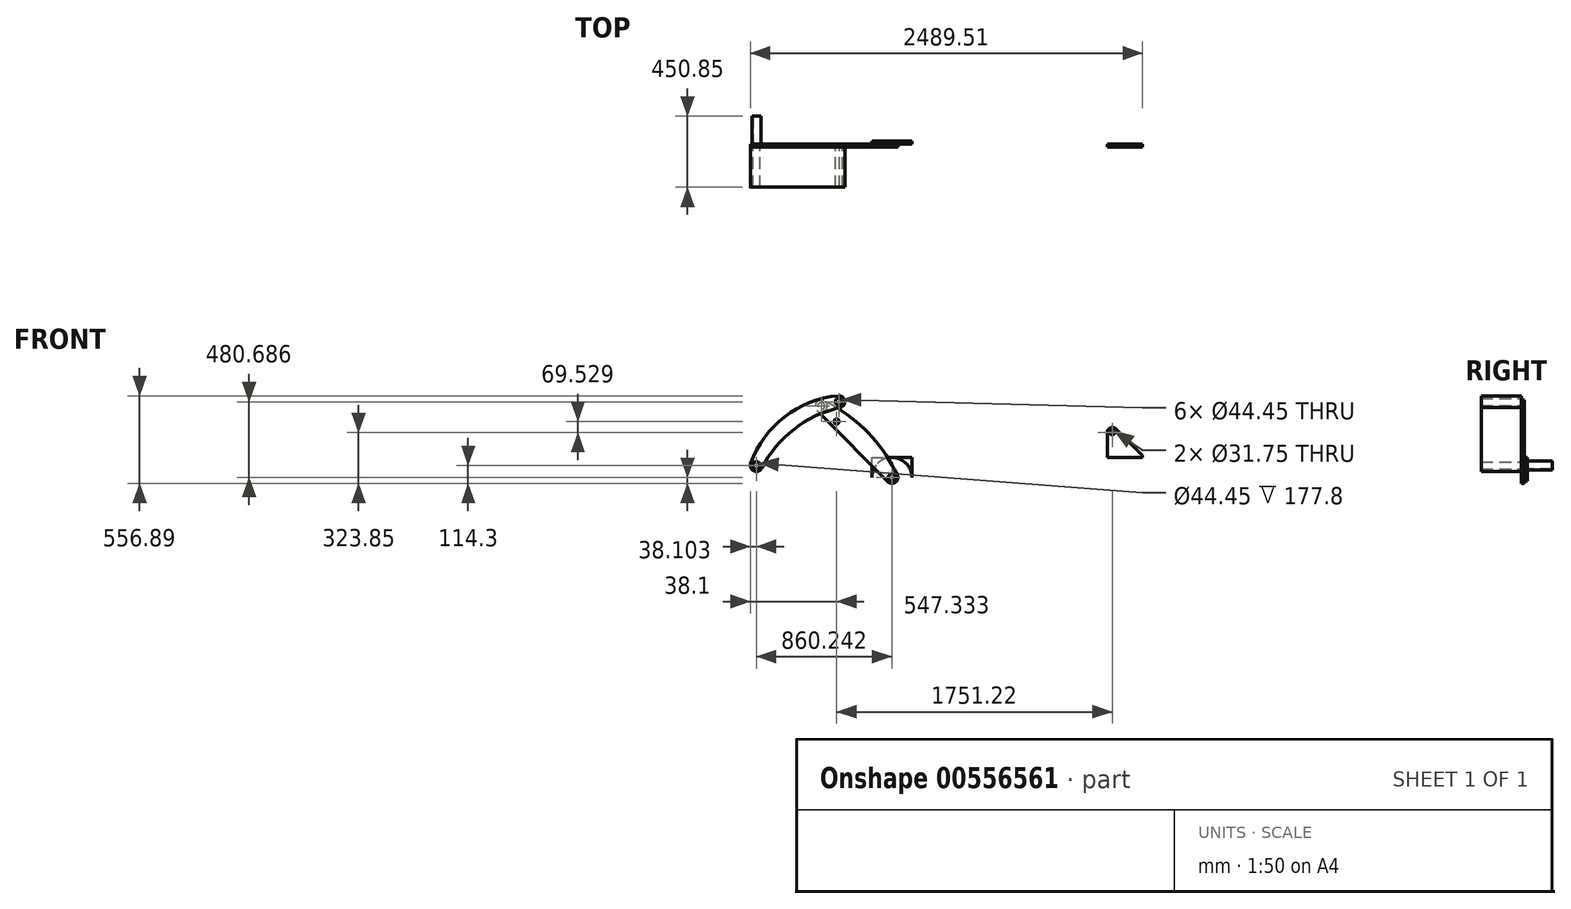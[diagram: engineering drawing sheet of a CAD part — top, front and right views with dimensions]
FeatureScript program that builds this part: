
annotation { "Feature Type Name" : "Feature", "Feature Type Description" : "" }
export const myFeature = defineFeature(function(context is Context, id is Id, definition is map)
    precondition{}
    {
        {
            var Q0;
            Q0=qCreatedBy(makeId("Front.planeOp"),FACE);
            var sketch = newSketch(context, id + "F0", { "sketchPlane" : qUnion([Q0])});
            skLineSegment(sketch, "E0.bottom", {"start": v(-1348.74, 177.8) * mm, "end": v(-129.54, 177.8) * mm, "construction": true});
            skLineSegment(sketch, "E0.top", {"start": v(-1348.74, 0) * mm, "end": v(-129.54, 0) * mm, "construction": true});
            skLineSegment(sketch, "E0.left", {"start": v(-1348.74, 177.8) * mm, "end": v(-1348.74, 0) * mm, "construction": true});
            skLineSegment(sketch, "E0.right", {"start": v(-129.54, 177.8) * mm, "end": v(-129.54, 0) * mm, "construction": true});
            skLineSegment(sketch, "E1.bottom", {"start": v(0, 177.8) * mm, "end": v(1219.2, 177.8) * mm, "construction": true});
            skLineSegment(sketch, "E1.top", {"start": v(0, 0) * mm, "end": v(1219.2, 0) * mm, "construction": true});
            skLineSegment(sketch, "E1.left", {"start": v(0, 177.8) * mm, "end": v(0, 0) * mm, "construction": true});
            skLineSegment(sketch, "E1.right", {"start": v(1219.2, 177.8) * mm, "end": v(1219.2, 0) * mm, "construction": true});
            skPoint(sketch, "E2", {"position": v(-64.77, 279.4) * mm});
            skPoint(sketch, "E3", {"position": v(-477, 127) * mm});
            skPoint(sketch, "E4", {"position": v(383.24, 50.8) * mm});
            skPoint(sketch, "E5", {"position": v(-64.77, 504.25) * mm});
            skCircle(sketch, "E6", {"center": v(-477, 127) * mm, "radius": 28.58 * mm, "construction": true});
            skCircle(sketch, "E7", {"center": v(383.24, 50.8) * mm, "radius": 28.58 * mm, "construction": true});
            skLineSegment(sketch, "E8", {"start": v(-477, 127) * mm, "end": v(-64.77, 504.25) * mm, "construction": true});
            skPoint(sketch, "E9", {"position": v(32.22, 406.08) * mm});
            skLineSegment(sketch, "E10", {"start": v(-64.77, 279.4) * mm, "end": v(-477, 127) * mm, "construction": true});
            skLineSegment(sketch, "E11", {"start": v(-64.77, 279.4) * mm, "end": v(347.47, 431.8) * mm, "construction": true});
            skLineSegment(sketch, "E12", {"start": v(347.47, 431.8) * mm, "end": v(906.03, 415.5) * mm, "construction": true});
            skPoint(sketch, "E13", {"position": v(792.84, 336.55) * mm});
            skLineSegment(sketch, "E14", {"start": v(792.84, 336.55) * mm, "end": v(1783.44, 336.55) * mm, "construction": true});
            skLineSegment(sketch, "E15", {"start": v(1783.44, 336.55) * mm, "end": v(32.22, 406.08) * mm, "construction": true});
            skLineSegment(sketch, "E16", {"start": v(906.03, 415.5) * mm, "end": v(792.84, 336.55) * mm, "construction": true});
            skLineSegment(sketch, "E17", {"start": v(792.84, 336.55) * mm, "end": v(383.24, 50.8) * mm, "construction": true});
            skLineSegment(sketch, "E18", {"start": v(383.24, 50.8) * mm, "end": v(32.22, 406.08) * mm, "construction": true});
            skLineSegment(sketch, "E19", {"start": v(32.22, 406.08) * mm, "end": v(-64.77, 504.25) * mm, "construction": true});
            skSolve(sketch);
        }
        {
            var Q0;
            Q0=qCreatedBy(makeId("Front.planeOp"),FACE);
            var sketch = newSketch(context, id + "F1", { "sketchPlane" : qUnion([Q0])});
            skCircle(sketch, "E20", {"center": v(-477, 127) * mm, "radius": 22.23 * mm});
            skCircle(sketch, "E21", {"center": v(-477, 127) * mm, "radius": 28.58 * mm});
            skSolve(sketch);
        }
        {
            var Q0;
            Q0 = qSketchRegion(id + "F1", true);
            extrude(context, id + "F2", {"entities" : qUnion([Q0]), "oppositeDirection" : true, "depth" : 177.8 * mm, "offsetDistance" : 25.4 * mm});
        }
        {
            var Q0;
            Q0=qCreatedBy(makeId("Front.planeOp"),FACE);
            var sketch = newSketch(context, id + "F3", { "sketchPlane" : qUnion([Q0])});
            skCircle(sketch, "E22", {"center": v(383.24, 50.8) * mm, "radius": 22.23 * mm});
            skArc(sketch, "E23", {"start": v(256.24, 50.8) * mm, "mid": v(383.24, 177.8) * mm, "end": v(510.24, 50.8) * mm});
            skLineSegment(sketch, "E24", {"start": v(510.24, 177.8) * mm, "end": v(510.24, 50.8) * mm});
            skLineSegment(sketch, "E25", {"start": v(256.24, 177.8) * mm, "end": v(510.24, 177.8) * mm});
            skLineSegment(sketch, "E26", {"start": v(256.24, 50.8) * mm, "end": v(256.24, 177.8) * mm});
            skSolve(sketch);
        }
        {
            var Q0;
            Q0 = qSketchRegion(id + "F3", true);
            extrude(context, id + "F4", {"entities" : qUnion([Q0]), "oppositeDirection" : true, "depth" : 19.05 * mm, "offsetDistance" : 25.4 * mm});
        }
        {
            var Q0;
            Q0=qCreatedBy(makeId("Front.planeOp"),FACE);
            var sketch = newSketch(context, id + "F5", { "sketchPlane" : qUnion([Q0])});
            skCircle(sketch, "E27", {"center": v(383.24, 50.8) * mm, "radius": 22.23 * mm});
            skArc(sketch, "E28", {"start": v(356.13, 24.02) * mm, "mid": v(405.17, 19.65) * mm, "end": v(417.59, 67.28) * mm});
            skCircle(sketch, "E29", {"center": v(32.22, 406.08) * mm, "radius": 15.88 * mm});
            skLineSegment(sketch, "E30.trimOffspring", {"start": v(146.95, 412.86) * mm, "end": v(146.95, 412.86) * mm});
            skArc(sketch, "E31", {"start": v(-47.87, 538.4) * mm, "mid": v(-95.66, 526.56) * mm, "end": v(-91.87, 477.47) * mm});
            skLineSegment(sketch, "E32", {"start": v(-91.87, 477.47) * mm, "end": v(356.13, 24.02) * mm});
            skCircle(sketch, "E33", {"center": v(-64.77, 504.25) * mm, "radius": 22.23 * mm});
            skArc(sketch, "E34", {"start": v(417.59, 67.28) * mm, "mid": v(224.32, 341.83) * mm, "end": v(-47.87, 538.4) * mm});
            skSolve(sketch);
        }
        {
            var Q0;
            Q0 = qSketchRegion(id + "F5", true);
            extrude(context, id + "F6", {"entities" : qUnion([Q0]), "depth" : 19.05 * mm, "offsetDistance" : 25.4 * mm});
        }
        {
            var Q0;
            Q0=qCreatedBy(makeId("Front.planeOp"),FACE);
            var sketch = newSketch(context, id + "F7", { "sketchPlane" : qUnion([Q0])});
            skCircle(sketch, "E35", {"center": v(-477, 127) * mm, "radius": 22.23 * mm});
            skCircle(sketch, "E36", {"center": v(-64.77, 504.25) * mm, "radius": 22.23 * mm});
            skArc(sketch, "E37", {"start": v(-512.9, 139.8) * mm, "mid": v(-492.12, 92.02) * mm, "end": v(-443.09, 109.64) * mm});
            skArc(sketch, "E38", {"start": v(-50.48, 468.93) * mm, "mid": v(-28.6, 516.2) * mm, "end": v(-74.34, 541.13) * mm});
            skArc(sketch, "E39", {"start": v(-74.34, 541.13) * mm, "mid": v(-343.48, 394.95) * mm, "end": v(-512.9, 139.8) * mm});
            skArc(sketch, "E40", {"start": v(-50.48, 468.93) * mm, "mid": v(-279.17, 324.68) * mm, "end": v(-443.09, 109.64) * mm});
            skLineSegment(sketch, "E41", {"start": v(847.43, 417.22) * mm, "end": v(780, 419.19) * mm, "construction": true});
            skLineSegment(sketch, "E42", {"start": v(847.43, 417.22) * mm, "end": v(906.03, 415.5) * mm, "construction": true});
            skCircle(sketch, "E43", {"center": v(-146.1, 406.71) * mm, "radius": 38.1 * mm, "construction": true});
            skLineSegment(sketch, "E44", {"start": v(-132.47, 442.3) * mm, "end": v(-182.75, 396.28) * mm, "construction": true});
            skLineSegment(sketch, "E45", {"start": v(-132.47, 442.3) * mm, "end": v(-43.7, 523.53) * mm, "construction": true});
            skSolve(sketch);
        }
        {
            var Q0;
            Q0 = qSketchRegion(id + "F7", true);
            extrude(context, id + "F8", {"entities" : qUnion([Q0]), "depth" : 19.05 * mm, "offsetDistance" : 25.4 * mm});
        }
        {
            var Q0;
            Q0=makeQuery(id+"F8.opExtrude","CAP_FACE",FACE,{"disambiguationData":[OSD([sQuery(id+"F7.wireOp",EDGE,"E36"),sQuery(id+"F7.wireOp",EDGE,"E37"),sQuery(id+"F7.wireOp",EDGE,"E38"),sQuery(id+"F7.wireOp",EDGE,"E39"),sQuery(id+"F7.wireOp",EDGE,"E40"),sQuery(id+"F7.wireOp",EDGE,"E35")])],"isStart":false});
            var sketch = newSketch(context, id + "F9", { "sketchPlane" : qUnion([Q0])});
            skCircle(sketch, "E46", {"center": v(46.24, 531.49) * mm, "radius": 22.23 * mm});
            skCircle(sketch, "E47", {"center": v(85.21, -73.5) * mm, "radius": 635 * mm, "construction": true});
            skCircle(sketch, "E48", {"center": v(235.26, -237.46) * mm, "radius": 762 * mm, "construction": true});
            skArc(sketch, "E49", {"start": v(49.5, 501.55) * mm, "mid": v(46.24, 531.49) * mm, "end": v(35.27, 559.53) * mm, "construction": true});
            skCircle(sketch, "E50", {"center": v(-477, 127) * mm, "radius": 22.23 * mm});
            skArc(sketch, "E51", {"start": v(-512.9, 139.8) * mm, "mid": v(-492.12, 92.02) * mm, "end": v(-443.09, 109.64) * mm});
            skArc(sketch, "E52", {"start": v(49.5, 493.53) * mm, "mid": v(84.2, 534.79) * mm, "end": v(42.9, 569.44) * mm});
            skArc(sketch, "E53", {"start": v(42.9, 569.44) * mm, "mid": v(-297.96, 436.06) * mm, "end": v(-512.9, 139.8) * mm});
            skArc(sketch, "E54", {"start": v(49.5, 493.53) * mm, "mid": v(-239.3, 356.12) * mm, "end": v(-443.09, 109.64) * mm});
            skSolve(sketch);
        }
        {
            var Q0;
            Q0 = qSketchRegion(id + "F9", true);
            extrude(context, id + "F10", {"entities" : qUnion([Q0]), "depth" : 254 * mm, "offsetDistance" : 25.4 * mm});
        }
        {
            var Q0;
            Q0=qCreatedBy(makeId("Front.planeOp"),FACE);
            var sketch = newSketch(context, id + "F11", { "sketchPlane" : qUnion([Q0])});
            skCircle(sketch, "E55", {"center": v(1783.44, 336.55) * mm, "radius": 15.88 * mm});
            skArc(sketch, "E56", {"start": v(1805.9, 359) * mm, "mid": v(1771.3, 365.88) * mm, "end": v(1751.7, 336.55) * mm});
            skLineSegment(sketch, "E57", {"start": v(1751.7, 336.55) * mm, "end": v(1751.7, 177.8) * mm});
            skLineSegment(sketch, "E58", {"start": v(1751.7, 177.8) * mm, "end": v(1974.4, 177.8) * mm});
            skLineSegment(sketch, "E59", {"start": v(1974.4, 190.5) * mm, "end": v(1805.9, 359) * mm});
            skLineSegment(sketch, "E60", {"start": v(1974.4, 190.5) * mm, "end": v(1974.4, 177.8) * mm});
            skSolve(sketch);
        }
        {
            var Q0;
            Q0 = qSketchRegion(id + "F11", true);
            extrude(context, id + "F12", {"entities" : qUnion([Q0]), "depth" : 19.05 * mm, "offsetDistance" : 25.4 * mm});
        }
    });
